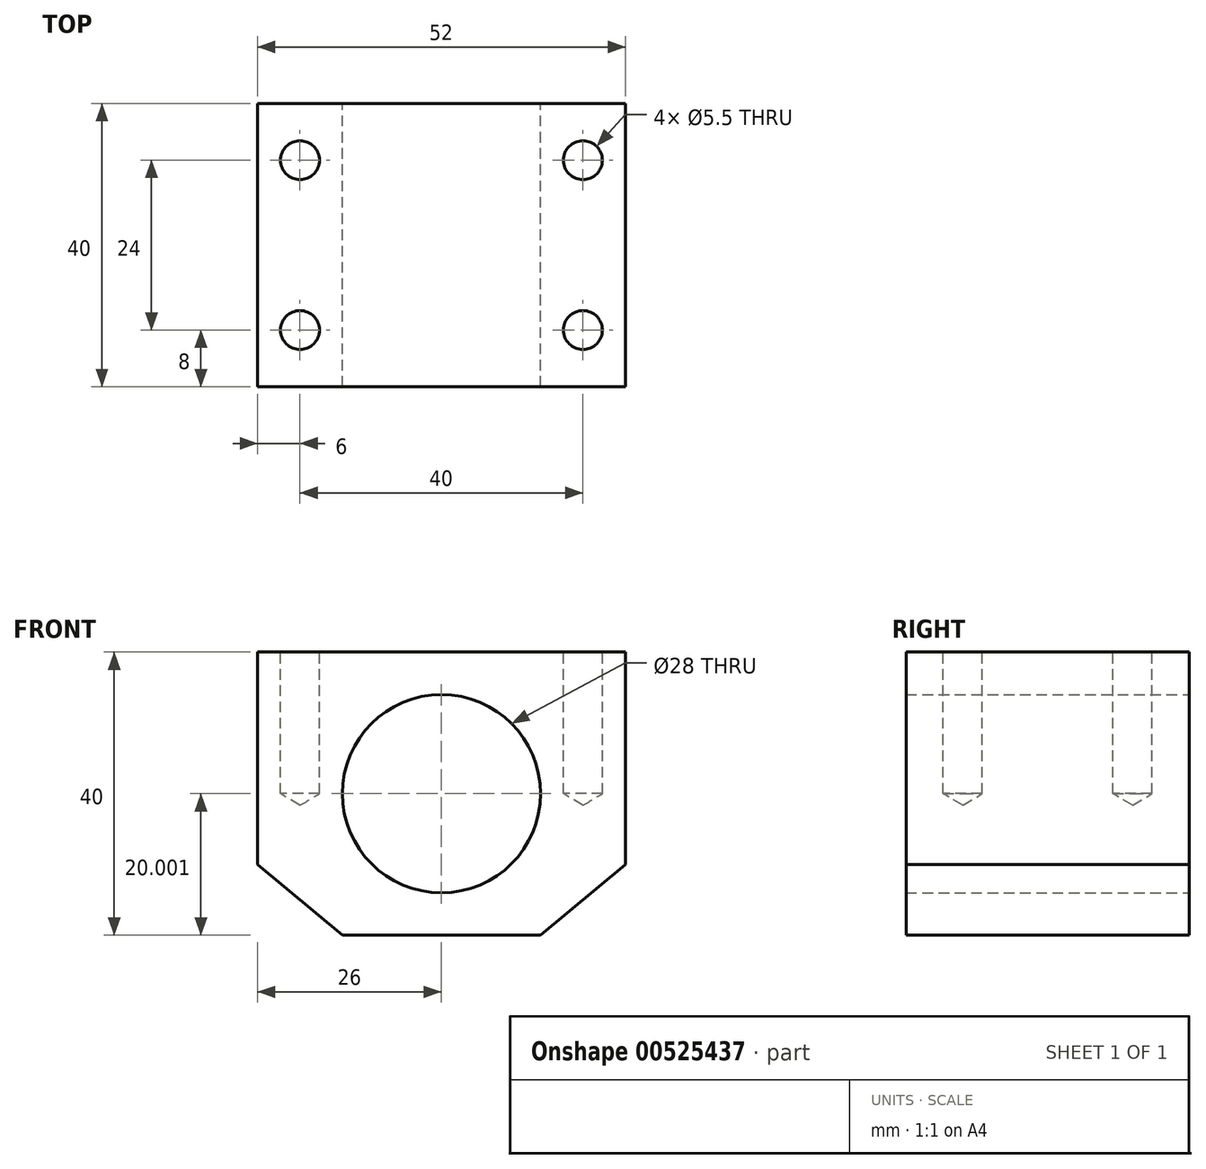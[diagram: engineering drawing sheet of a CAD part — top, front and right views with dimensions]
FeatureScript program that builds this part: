
annotation { "Feature Type Name" : "Feature", "Feature Type Description" : "" }
export const myFeature = defineFeature(function(context is Context, id is Id, definition is map)
    precondition{}
    {
        {
            var Q0;
            Q0=qCreatedBy(makeId("Front.planeOp"),FACE);
            var sketch = newSketch(context, id + "F0", { "sketchPlane" : qUnion([Q0])});
            skLineSegment(sketch, "E0", {"start": v(-26, 22.78) * mm, "end": v(26, 22.78) * mm});
            skLineSegment(sketch, "E1", {"start": v(26, 22.78) * mm, "end": v(26, -7.22) * mm});
            skLineSegment(sketch, "E2", {"start": v(26, -7.22) * mm, "end": v(14, -17.22) * mm});
            skLineSegment(sketch, "E3", {"start": v(14, -17.22) * mm, "end": v(-14, -17.22) * mm});
            skLineSegment(sketch, "E4", {"start": v(-14, -17.22) * mm, "end": v(-26, -7.22) * mm});
            skLineSegment(sketch, "E5", {"start": v(-26, -7.22) * mm, "end": v(-26, 22.78) * mm});
            skPoint(sketch, "E6", {"position": v(0, 2.78) * mm});
            skSolve(sketch);
        }
        {
            var Q0;
            Q0 = qSketchRegion(id + "F0", true);
            extrude(context, id + "F1", {"entities" : qUnion([Q0]), "depth" : 40 * mm, "offsetDistance" : 25 * mm});
        }
        {
            var Q0;
            Q0=sQuery(id+"F0.wireOp",VERTEX,"E6");
            var Q1;
            Q1=makeQuery(id+"F1.opExtrude","SWEPT_BODY",BODY,{"disambiguationData":[OSD([sQuery(id+"F0.wireOp",EDGE,"E0"),sQuery(id+"F0.wireOp",EDGE,"E1"),sQuery(id+"F0.wireOp",EDGE,"E2"),sQuery(id+"F0.wireOp",EDGE,"E3"),sQuery(id+"F0.wireOp",EDGE,"E4"),sQuery(id+"F0.wireOp",EDGE,"E5")])]});
            hole(context, id + "F2", {"style" : HoleStyle.SIMPLE, "endStyle" : HoleEndStyle.THROUGH, "oppositeDirection" : true, "holeDiameter" : 28 * mm, "isTappedThrough" : true, "tappedDepth" : 12 * mm, "tapClearance" : 3, "locations" : qUnion([Q0]), "scope" : qUnion([Q1]), "majorDiameter" : 5 * mm});
        }
        {
            var Q0;
            Q0=makeQuery(id+"F1.opExtrude","SWEPT_FACE",FACE,{"disambiguationData":[OSD([sQuery(id+"F0.wireOp",EDGE,"E0")])]});
            var sketch = newSketch(context, id + "F3", { "sketchPlane" : qUnion([Q0])});
            skPoint(sketch, "E7", {"position": v(-20, -8) * mm});
            skPoint(sketch, "E8", {"position": v(20, -8) * mm});
            skPoint(sketch, "E9", {"position": v(20, -32) * mm});
            skPoint(sketch, "E10", {"position": v(-20, -32) * mm});
            skSolve(sketch);
        }
        {
            var Q0;
            Q0=sQuery(id+"F3.wireOp",VERTEX,"E7");
            var Q1;
            Q1=sQuery(id+"F3.wireOp",VERTEX,"E10");
            var Q2;
            Q2=sQuery(id+"F3.wireOp",VERTEX,"E9");
            var Q3;
            Q3=sQuery(id+"F3.wireOp",VERTEX,"E8");
            var Q4;
            Q4=makeQuery(id+"F1.opExtrude","SWEPT_BODY",BODY,{"disambiguationData":[OSD([sQuery(id+"F0.wireOp",EDGE,"E0"),sQuery(id+"F0.wireOp",EDGE,"E1"),sQuery(id+"F0.wireOp",EDGE,"E2"),sQuery(id+"F0.wireOp",EDGE,"E3"),sQuery(id+"F0.wireOp",EDGE,"E4"),sQuery(id+"F0.wireOp",EDGE,"E5")])]});
            hole(context, id + "F4", {"style" : HoleStyle.SIMPLE, "endStyle" : HoleEndStyle.BLIND, "standardTappedOrClearance" : lookupTablePath({ "standard" : "ISO", "fit" : "Normal", "size" : "M5", "type" : "Clearance" }), "standardBlindInLast" : lookupTablePath({ "fit" : "Standard", "standard" : "ISO", "size" : "M5", "type" : "Clearance" }), "holeDiameter" : 5.5 * mm, "holeDepth" : 20 * mm, "isTappedThrough" : true, "tappedDepth" : 12 * mm, "tapClearance" : 3, "locations" : qUnion([Q0, Q1, Q2, Q3]), "scope" : qUnion([Q4])});
        }
    });
